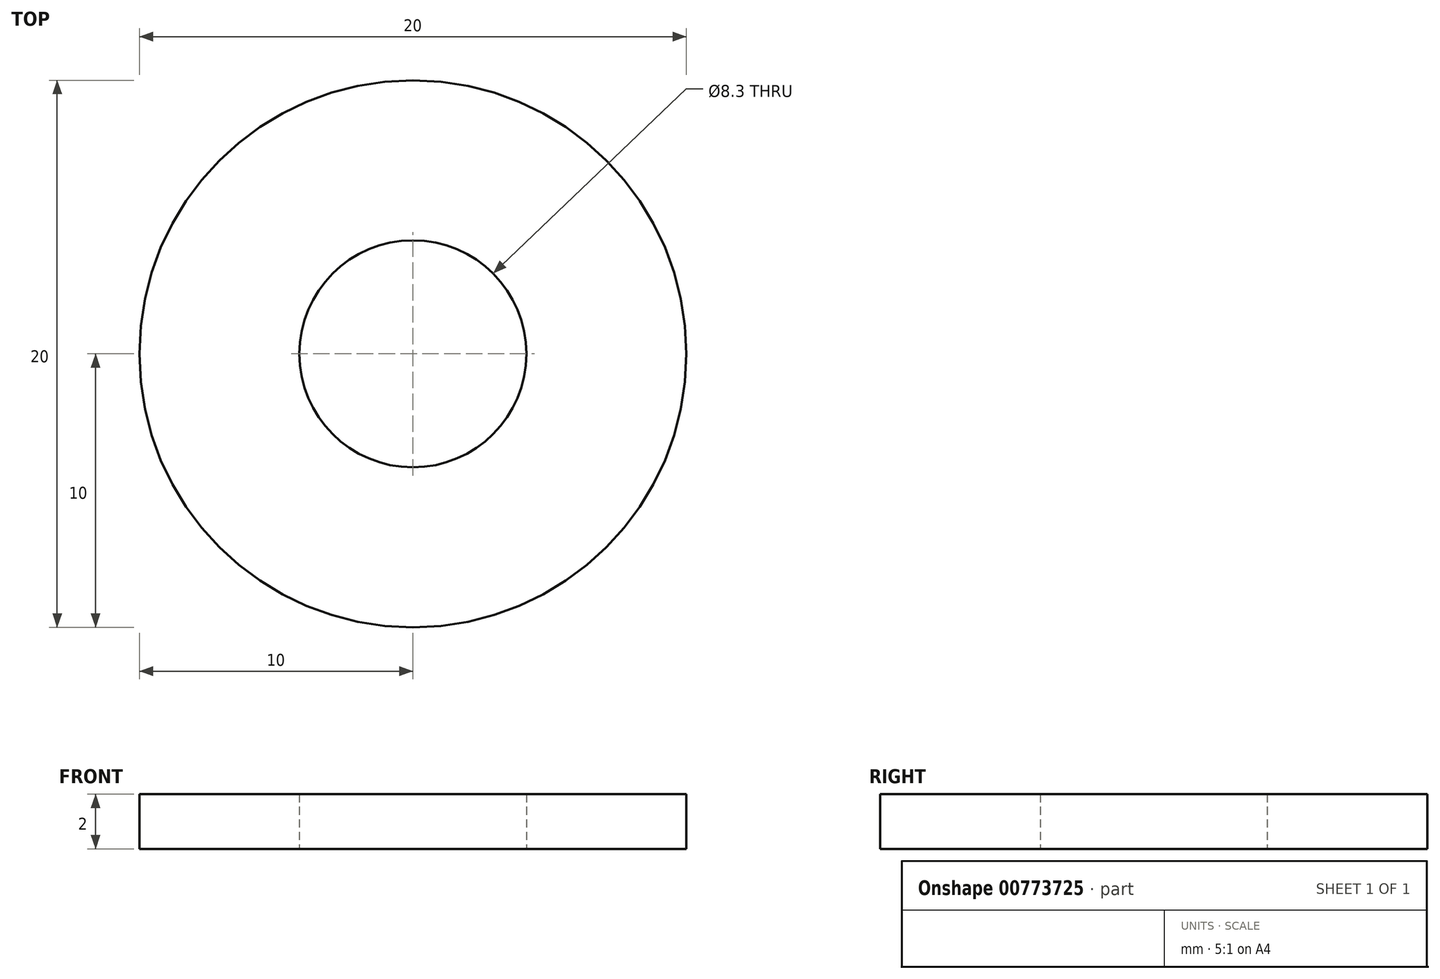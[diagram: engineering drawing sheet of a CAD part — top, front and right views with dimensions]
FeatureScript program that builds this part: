
annotation { "Feature Type Name" : "Feature", "Feature Type Description" : "" }
export const myFeature = defineFeature(function(context is Context, id is Id, definition is map)
    precondition{}
    {
        {
            assignVariable(context, id + "F0", {"name" : "spacerthick", "anyValue" : 2});
        }
        {
            var Q0;
            Q0=qCreatedBy(makeId("Top.planeOp"),FACE);
            var sketch = newSketch(context, id + "F1", { "sketchPlane" : qUnion([Q0])});
            skCircle(sketch, "E0", {"center": v(0, 0) * mm, "radius": 4.15 * mm});
            skCircle(sketch, "E1", {"center": v(0, 0) * mm, "radius": 10 * mm});
            skSolve(sketch);
        }
        {
            var Q0;
            Q0 = qSketchRegion(id + "F1", true);
            extrude(context, id + "F2", {"entities" : qUnion([Q0]), "depth" : (getVariable(context, 'spacerthick')) * mm, "offsetDistance" : 25 * mm});
        }
    });
